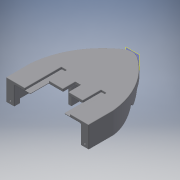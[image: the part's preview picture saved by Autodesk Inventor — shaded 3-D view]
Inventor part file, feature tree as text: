
AUTODESK INVENTOR PART (.ipt)
format: ipt  version: 2018 (Build 220112000, 112)  size: 1,168,896 bytes
history: native  units: mm
features: projected_geometry x66, reference x34, extrude x25, sketch x25, fillet x17, other x15, plane x5
ambient origin geometry x8: Origin, YZ Plane, XZ Plane, XY Plane, X Axis, Y Axis, Z Axis, Center Point
bodies: Solid1 (feature_tree)
feature tree (187):
  extrude  "Extrusion1"  Depth=40.0mm
  sketch  "Sketch3"  dims[d4=110.0mm d5=130.0mm]
  plane  "Work Plane1"
  extrude  "Extrusion2"  Depth=130.0mm
  extrude  "Extrusion3"  Depth=20.0mm
  extrude  "Extrusion4"  Depth=10.0mm TaperAngle=0.0deg
  extrude  "Extrusion5"  Depth=20.0mm
  extrude  "Extrusion6"  Depth=10.0mm
  extrude  "Extrusion7"  Depth=50.0mm
  extrude  "Extrusion8"  Depth=35.0mm TaperAngle=0.0deg
  extrude  "Extrusion9"  Depth=5.0mm TaperAngle=0.0deg
  fillet  "Fillet1"  Radius=160.0mm
  extrude  "Extrusion10"  Depth=20.0mm TaperAngle=0.0deg
  extrude  "Extrusion11"  Depth=160.0mm TaperAngle=0.0deg
  extrude  "Extrusion12"  Depth=6.0mm
  sketch  "Sketch16"  dims[d72=160.0mm d73=0.0mm d74=6.0mm]
  plane  "Work Plane2"
  extrude  "Extrusion13"  Depth=1.0mm
  fillet  "Fillet2"  Radius=60.0mm
  fillet  "Fillet3"  Radius=1.0mm
  fillet  "Fillet4"  Radius=8.35mm
  fillet  "Fillet5"  Radius=10.0mm
  extrude  "Extrusion14"  Depth=4.118mm
  fillet  "Fillet6"  Radius=4.572mm
  plane  "Work Plane3"
  extrude  "Extrusion15"  Depth=16.002mm
  extrude  "Extrusion16"  Depth=10.0mm TaperAngle=0.0deg
  sketch  "Sketch20"  dims[d87=2.94mm d88=16.002mm]
  plane  "Work Plane4"
  extrude  "Extrusion17"  Depth=1.0mm
  sketch  "Sketch21"  dims[d89=8.0mm d90=10.0mm d91=0.0mm]
  plane  "Work Plane5"
  extrude  "Extrusion18"  Depth=1.0mm
  fillet  "Fillet8"  Radius=1.0mm
  fillet  "Fillet9"  Radius=1.0mm
  fillet  "Fillet10"  Radius=10.0mm
  fillet  "Fillet11"  Radius=1.0mm
  fillet  "Fillet12"  Radius=10.0mm
  fillet  "Fillet13"  Radius=5.0mm
  sketch  "Sketch22"  dims[d92=1.0mm d93=1.0mm]
  extrude  "Extrusion21"  Depth=5.0mm
  fillet  "Fillet16"  Radius=18.0mm
  extrude  "Extrusion22"  Depth=10.0mm TaperAngle=0.0deg
  extrude  "Extrusion23"  Depth=20.0mm
  fillet  "Fillet17"  Radius=19.5mm
  extrude  "Extrusion24"  Depth=2.0mm
  extrude  "Extrusion25"  Depth=2.4mm
  extrude  "Extrusion26"  Depth=2.0mm
  fillet  "Fillet18"  Radius=4.0mm
  fillet  "Fillet19"  Radius=2.0mm
  fillet  "Fillet20"  Radius=4.0mm
  extrude  "Extrusion29"  Depth=10.0mm TaperAngle=0.0deg
  sketch  "Sketch1"  dims[d2=40.0mm d3=40.0mm]
  reference  "Reference1"
  reference  "Reference2"
  other  "Work Point1"
  sketch  "Sketch5"  dims[d6=130.0mm d7=20.0mm]
  sketch  "Sketch6"  dims[d8=20.0mm d9=10.0mm d10=0.0mm]
  sketch  "Sketch8"  dims[d17=40.0mm d18=20.0mm]
  sketch  "Sketch9"  dims[d19=40.0mm d20=10.0mm]
  projected_geometry  "Projected Loop1"
  projected_geometry  "Projected Loop2"
  projected_geometry  "Projected Loop3"
  projected_geometry  "Projected Loop4"
  sketch  "Sketch10"  dims[d21=50.0mm d22=50.0mm]
  sketch  "Sketch11"  dims[d23=35.0mm d24=0.0mm d25=25.0mm d26=0.0mm]
  sketch  "Sketch12"  dims[d27=160.0mm d28=0.0mm]
  reference  "Reference3"
  reference  "Reference4"
  reference  "Reference5"
  reference  "Reference6"
  reference  "Reference7"
  projected_geometry  "Projected Loop5"
  projected_geometry  "Projected Loop6"
  sketch  "Sketch13"  dims[d53=36.0mm d54=36.0mm d55=99.0mm d56=117.0mm d57=117.0mm d58=18.0mm d59=18.0mm d60=160.0mm d61=5.0mm d62=0.0mm d63=0.0mm d64=160.0mm d65=0.0mm]
  projected_geometry  "Projected Loop7"
  sketch  "Sketch14"  dims[d66=20.0mm d67=12.5mm d68=0.0mm]
  reference  "Reference8"
  sketch  "Sketch15"  dims[d69=25.0mm d70=160.0mm d71=0.0mm]
  reference  "Reference9"
  reference  "Reference10"
  reference  "Reference11"
  reference  "Reference12"
  reference  "Reference13"
  reference  "Reference14"
  reference  "Reference15"
  projected_geometry  "Projected Loop8"
  reference  "Reference16"
  reference  "Reference17"
  reference  "Reference18"
  reference  "Reference19"
  reference  "Reference20"
  reference  "Reference21"
  reference  "Reference22"
  reference  "Reference23"
  reference  "Reference24"
  reference  "Reference25"
  reference  "Reference26"
  reference  "Reference27"
  sketch  "Sketch17"  dims[d75=40.0mm d76=0.0mm d77=1.0mm d78=60.0mm d79=0.0mm d80=1.0mm d81=8.35mm d82=10.0mm d83=0.0mm]
  reference  "Reference28"
  reference  "Reference29"
  reference  "Reference30"
  projected_geometry  "Projected Loop9"
  projected_geometry  "Projected Loop10"
  projected_geometry  "Projected Loop11"
  projected_geometry  "Projected Loop12"
  projected_geometry  "Projected Loop13"
  projected_geometry  "Projected Loop14"
  projected_geometry  "Projected Loop15"
  projected_geometry  "Projected Loop16"
  projected_geometry  "Projected Loop17"
  projected_geometry  "Projected Loop18"
  projected_geometry  "Projected Loop19"
  projected_geometry  "Projected Loop20"
  projected_geometry  "Projected Loop21"
  projected_geometry  "Projected Loop22"
  projected_geometry  "Projected Loop23"
  projected_geometry  "Projected Loop24"
  projected_geometry  "Projected Loop25"
  projected_geometry  "Projected Loop26"
  projected_geometry  "Projected Loop27"
  projected_geometry  "Projected Loop28"
  projected_geometry  "Projected Loop29"
  projected_geometry  "Projected Loop30"
  projected_geometry  "Projected Loop31"
  projected_geometry  "Projected Loop32"
  projected_geometry  "Projected Loop33"
  projected_geometry  "Projected Loop34"
  projected_geometry  "Projected Loop35"
  projected_geometry  "Projected Loop36"
  projected_geometry  "Projected Loop37"
  projected_geometry  "Projected Loop38"
  projected_geometry  "Projected Loop39"
  projected_geometry  "Projected Loop40"
  projected_geometry  "Projected Loop41"
  projected_geometry  "Projected Loop42"
  projected_geometry  "Projected Loop43"
  projected_geometry  "Projected Loop44"
  projected_geometry  "Projected Loop45"
  projected_geometry  "Projected Loop46"
  projected_geometry  "Projected Loop47"
  projected_geometry  "Projected Loop48"
  projected_geometry  "Projected Loop49"
  projected_geometry  "Projected Loop50"
  projected_geometry  "Projected Loop51"
  projected_geometry  "Projected Loop52"
  projected_geometry  "Projected Loop53"
  projected_geometry  "Projected Loop54"
  projected_geometry  "Projected Loop55"
  projected_geometry  "Projected Loop56"
  projected_geometry  "Projected Loop57"
  projected_geometry  "Projected Loop58"
  projected_geometry  "Projected Loop59"
  projected_geometry  "Projected Loop60"
  projected_geometry  "Projected Loop61"
  projected_geometry  "Projected Loop62"
  sketch  "Sketch19"  dims[d84=0.2mm d85=4.118mm d86=4.572mm]
  reference  "Reference31"
  projected_geometry  "Projected Loop63"
  projected_geometry  "Projected Loop64"
  projected_geometry  "Projected Loop65"
  projected_geometry  "Projected Loop66"
  reference  "Reference33"
  sketch  "Sketch24"  dims[d94=1.0mm d95=1.0mm d96=1.0mm d97=1.0mm d98=10.0mm d99=0.0mm d100=1.0mm d101=10.0mm d102=0.0mm d103=5.0mm]
  reference  "Reference34"
  sketch  "Sketch25"  dims[d104=5.0mm d105=2.5mm d106=18.0mm]
  reference  "Reference35"
  sketch  "Sketch26"  dims[d107=2.5mm d108=10.0mm d109=0.0mm]
  sketch  "Sketch27"  dims[d110=20.0mm d111=9.75mm d112=19.5mm]
  sketch  "Sketch28"  dims[d113=2.0mm d114=0.2mm]
  sketch  "Sketch29"  dims[d115=0.2mm d116=2.4mm]
  sketch  "Sketch33"  dims[d117=2.0mm d118=2.0mm d119=4.0mm d120=2.0mm d121=4.0mm d122=10.0mm d123=0.0mm d124=25.5mm d125=10.0mm d126=0.0mm d128=1.0mm d129=1.0mm d130=1.0mm d131=1.0mm d132=1.0mm d133=0.5mm d134=30.0mm d135=30.0mm d136=2.0mm d137=2.0mm d138=5.0mm d139=20.0mm d140=5.0mm d141=20.0mm d142=4.85mm d143=9.7mm d144=3.0mm d153=10.0mm d154=0.0mm d155=1.0mm d156=2.75mm d157=10.0mm d158=0.0mm d159=70.0mm d160=25.0mm d161=10.0mm d162=0.0mm d163=1.0mm d164=30.0mm d165=4.0mm d166=8.0mm d167=20.0mm d168=100.0mm d169=0.0mm d170=100.0mm d171=0.0mm d172=0.25mm d173=0.25mm d174=0.25mm d175=0.25mm d176=100.0mm d177=0.0mm d178=1.0mm d179=1.0mm d180=1.0mm d181=13.8mm d194=2.5mm d195=0.25mm d196=2.5mm d197=2.0mm d198=0.25mm d199=2.0mm d200=0.5mm d201=1.0mm d202=0.0mm]
  other  "<userpath>\OneDrive\Documents\Inventor\TSA\2018\Animatronics\Tortoise\Head\HeadAssembly.iam"
  other  "HeadAssembly.iam"
  other  "HeadBase:1"
  other  "Rack:2"
  other  "Rack:1"
  other  "HeadTop:1"
  other  "<userpath>\OneDrive\Documents\Inventor\TSA\2018\Animatronics\Tortoise\TurtleAssembly.iam"
  other  "TurtleAssembly.iam"
  other  "servo (2):4"
  other  "servo (2):5"
  other  "SyringeConnector:1"
  other  "Syringe:2"
  other  "SyringEnd:1"
  other  "FlexHinge:1"
